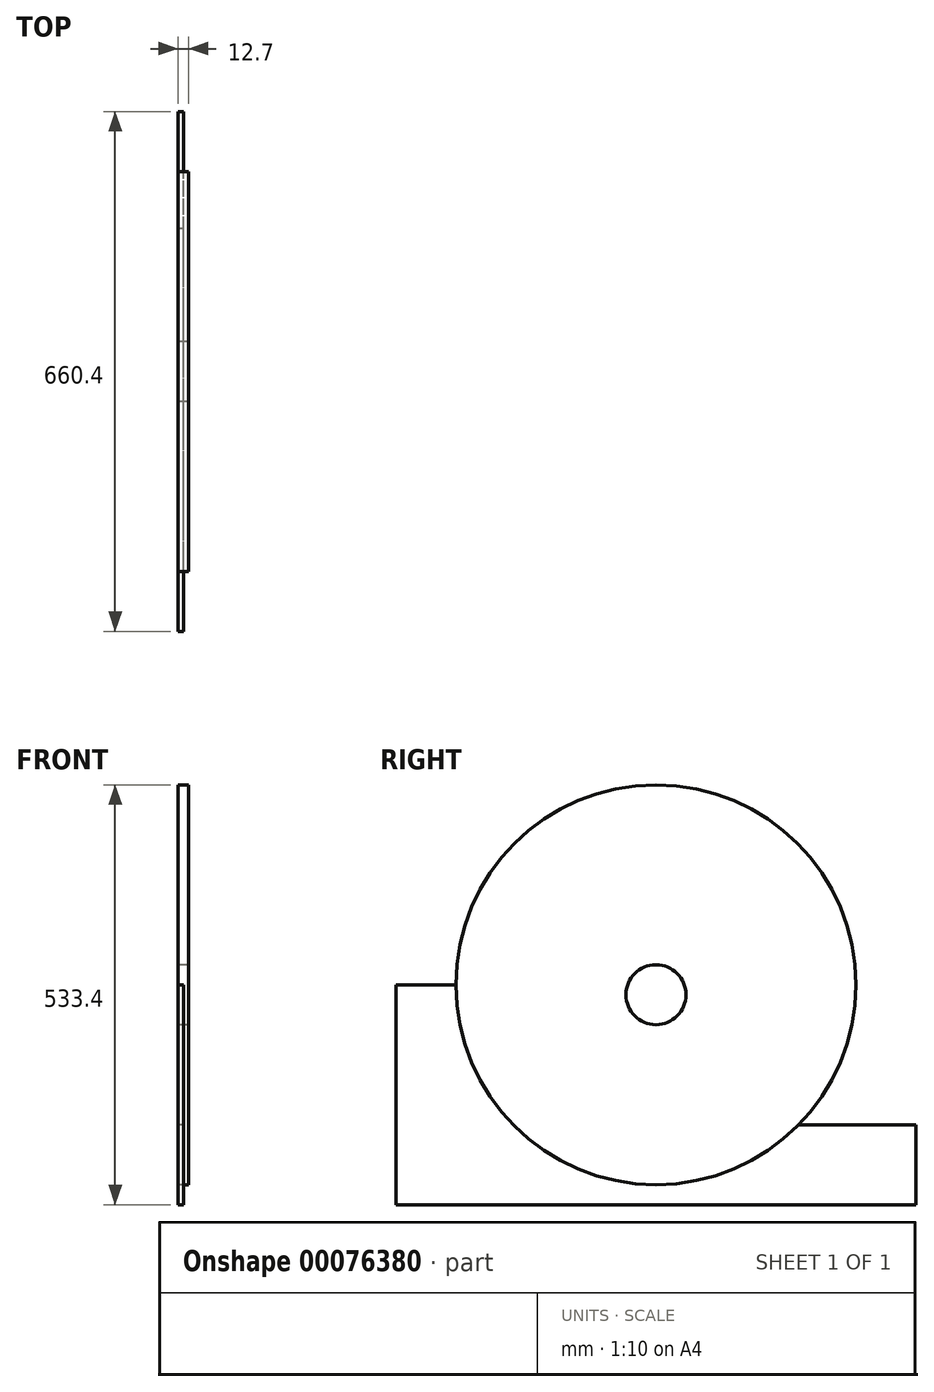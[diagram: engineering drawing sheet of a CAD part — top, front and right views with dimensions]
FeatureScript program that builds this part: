
annotation { "Feature Type Name" : "Feature", "Feature Type Description" : "" }
export const myFeature = defineFeature(function(context is Context, id is Id, definition is map)
    precondition{}
    {
        {
            var Q0;
            Q0=qCreatedBy(makeId("Right.planeOp"),FACE);
            var sketch = newSketch(context, id + "F0", { "sketchPlane" : qUnion([Q0])});
            skLineSegment(sketch, "E0.bottom", {"start": v(-330.2, 126.79) * mm, "end": v(330.2, 126.79) * mm});
            skLineSegment(sketch, "E0.top", {"start": v(-330.2, -152.61) * mm, "end": v(330.2, -152.61) * mm});
            skLineSegment(sketch, "E0.left", {"start": v(-330.2, 126.79) * mm, "end": v(-330.2, -152.61) * mm});
            skLineSegment(sketch, "E0.right", {"start": v(330.2, 126.79) * mm, "end": v(330.2, -152.61) * mm});
            skCircle(sketch, "E1", {"center": v(0, 126.79) * mm, "radius": 254 * mm});
            skLineSegment(sketch, "E2", {"start": v(181.4, -51.01) * mm, "end": v(330.2, -51.01) * mm});
            skCircle(sketch, "E3", {"center": v(0, 114.09) * mm, "radius": 38.1 * mm});
            skSolve(sketch);
        }
        {
            var Q0;
            {var subQ1=sQuery(id+"F0.wireOp",EDGE,"E0.top");Q0=makeQuery(id+"F0.imprint","IMPRINT",FACE,{"disambiguationData":[TD([[makeQuery(id+"F0.imprint","IMPRINT",EDGE,{"derivedFrom":subQ1}),1.0]])]});}
            extrude(context, id + "F1", {"entities" : qUnion([Q0]), "depth" : 6.35 * mm});
        }
        {
            var Q0;
            {var subQ0=sQuery(id+"F0.wireOp",EDGE,"E3");var subQ1=sQuery(id+"F0.wireOp",EDGE,"E0.bottom");var subQ2=makeQuery(id+"F0.imprint","INTERSECT",VERTEX,{"disambiguationData":[OD(0.0)],"derivedFrom":[subQ1,subQ0]});Q0=makeQuery(id+"F0.imprint","IMPRINT",FACE,{"disambiguationData":[TD([[makeQuery(id+"F0.imprint","IMPRINT",EDGE,{"disambiguationData":[TD([[subQ2,-1.0]])],"derivedFrom":subQ1}),1.0]])]});}
            var Q1;
            {var subQ0=sQuery(id+"F0.wireOp",EDGE,"E3");var subQ1=sQuery(id+"F0.wireOp",EDGE,"E0.bottom");var subQ2=makeQuery(id+"F0.imprint","INTERSECT",VERTEX,{"disambiguationData":[OD(0.0)],"derivedFrom":[subQ1,subQ0]});Q1=makeQuery(id+"F0.imprint","IMPRINT",FACE,{"disambiguationData":[TD([[makeQuery(id+"F0.imprint","IMPRINT",EDGE,{"disambiguationData":[TD([[subQ2,-1.0]])],"derivedFrom":subQ1}),-1.0]])]});}
            extrude(context, id + "F2", {"entities" : qUnion([Q0, Q1]), "depth" : 12.7 * mm});
        }
    });
